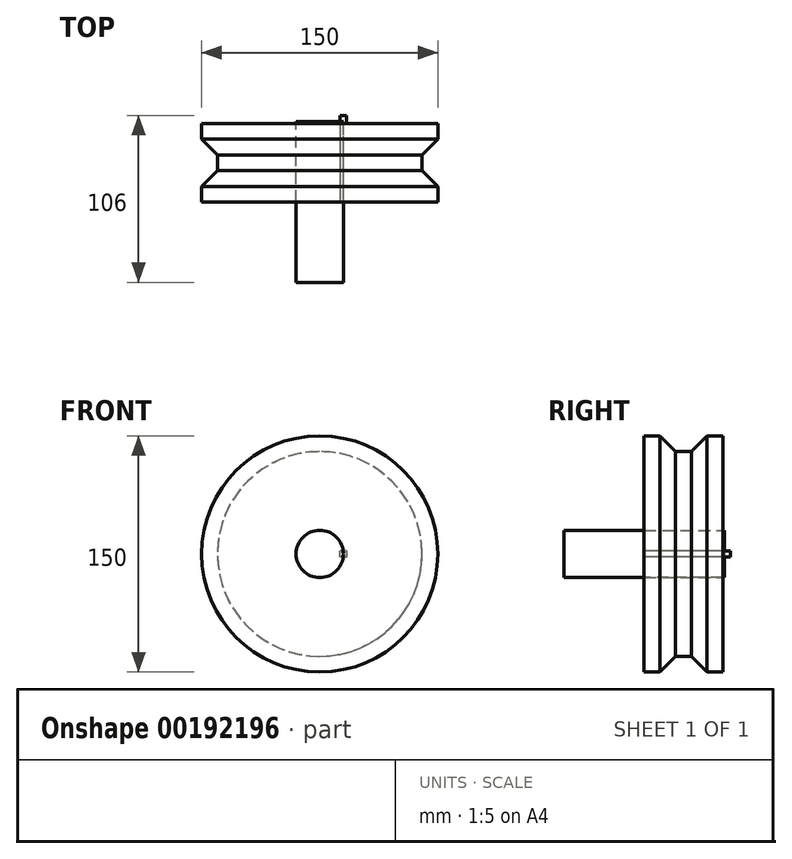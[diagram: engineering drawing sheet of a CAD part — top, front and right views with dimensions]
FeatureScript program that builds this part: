
annotation { "Feature Type Name" : "Feature", "Feature Type Description" : "" }
export const myFeature = defineFeature(function(context is Context, id is Id, definition is map)
    precondition{}
    {
        {
            var Q0;
            Q0=qCreatedBy(makeId("Front.planeOp"),FACE);
            var sketch = newSketch(context, id + "F0", { "sketchPlane" : qUnion([Q0])});
            skCircle(sketch, "E0", {"center": v(0, 0) * mm, "radius": 65 * mm});
            skSolve(sketch);
        }
        {
            var Q0;
            Q0 = qSketchRegion(id + "F0", true);
            var Q1;
            Q1 = qSketchRegion(id + "F4", true);
            extrude(context, id + "F1", {"entities" : qUnion([Q0, Q1]), "depth" : 10 * mm, "symmetric" : true});
        }
        {
            var Q0;
            Q0=makeQuery(id+"F1.opExtrude","CAP_FACE",FACE,{"disambiguationData":[OSD([sQuery(id+"F0.wireOp",EDGE,"E0")])],"isStart":false});
            var sketch = newSketch(context, id + "F2", { "sketchPlane" : qUnion([Q0])});
            skCircle(sketch, "E1", {"center": v(0, 0) * mm, "radius": 75 * mm});
            skSolve(sketch);
        }
        {
            var Q0;
            Q0 = qSketchRegion(id + "F2", true);
            extrude(context, id + "F3", {"entities" : qUnion([Q0]), "operationType" : NewBodyOperationType.ADD, "depth" : 20 * mm});
        }
        {
            var Q0;
            Q0=makeQuery(id+"F1.opExtrude","CAP_FACE",FACE,{"disambiguationData":[OSD([sQuery(id+"F0.wireOp",EDGE,"E0")])],"isStart":true});
            var sketch = newSketch(context, id + "F4", { "sketchPlane" : qUnion([Q0])});
            skCircle(sketch, "E2", {"center": v(0, 0) * mm, "radius": 75 * mm});
            skSolve(sketch);
        }
        {
            var Q0;
            Q0 = qSketchRegion(id + "F4", true);
            extrude(context, id + "F5", {"entities" : qUnion([Q0]), "operationType" : NewBodyOperationType.ADD, "depth" : 20 * mm});
        }
        {
            var Q0;
            Q0=makeQuery(id+"F3.opExtrude","CAP_EDGE",EDGE,{"disambiguationData":[OSD([sQuery(id+"F2.wireOp",EDGE,"E1")])],"isStart":true});
            var Q1;
            Q1=makeQuery(id+"F5.opExtrude","CAP_EDGE",EDGE,{"disambiguationData":[OSD([sQuery(id+"F4.wireOp",EDGE,"E2")])],"isStart":true});
            chamfer(context, id + "F6", {"entities" : qUnion([Q0, Q1]), "width" : 10 * mm, "tangentPropagation" : true});
        }
        {
            var Q0;
            Q0=makeQuery(id+"F3.opExtrude","CAP_FACE",FACE,{"disambiguationData":[OSD([sQuery(id+"F2.wireOp",EDGE,"E1")])],"isStart":false});
            var sketch = newSketch(context, id + "F7", { "sketchPlane" : qUnion([Q0])});
            skCircle(sketch, "E3", {"center": v(0, 0) * mm, "radius": 15 * mm});
            skSolve(sketch);
        }
        {
            var Q0;
            Q0 = qSketchRegion(id + "F7", true);
            extrude(context, id + "F8", {"entities" : qUnion([Q0]), "operationType" : NewBodyOperationType.REMOVE, "oppositeDirection" : true, "depth" : 53.4 * mm});
        }
        {
            var Q0;
            Q0=makeQuery(id+"F3.opExtrude","CAP_FACE",FACE,{"disambiguationData":[OSD([sQuery(id+"F2.wireOp",EDGE,"E1")])],"isStart":false});
            var sketch = newSketch(context, id + "F9", { "sketchPlane" : qUnion([Q0])});
            skLineSegment(sketch, "E4.bottom", {"start": v(17, -2) * mm, "end": v(13, -2) * mm});
            skLineSegment(sketch, "E4.top", {"start": v(17, 2) * mm, "end": v(13, 2) * mm});
            skLineSegment(sketch, "E4.left", {"start": v(17, -2) * mm, "end": v(17, 2) * mm});
            skLineSegment(sketch, "E4.right", {"start": v(13, -2) * mm, "end": v(13, 2) * mm});
            skPoint(sketch, "E4.middle", {"position": v(15, 0) * mm});
            skSolve(sketch);
        }
        {
            var Q0;
            Q0 = qSketchRegion(id + "F9", true);
            extrude(context, id + "F10", {"entities" : qUnion([Q0]), "operationType" : NewBodyOperationType.ADD, "oppositeDirection" : true, "depth" : 55 * mm});
        }
        {
            var Q0;
            Q0=makeQuery(id+"F10.boolean.opBoolean","MERGE",FACE,{"derivedFrom":[makeQuery(id+"F3.opExtrude","CAP_FACE",FACE,{"disambiguationData":[OSD([sQuery(id+"F2.wireOp",EDGE,"E1")])],"isStart":false}),makeQuery(id+"F10.opExtrude","CAP_FACE",FACE,{"disambiguationData":[OSD([sQuery(id+"F9.wireOp",EDGE,"E4.bottom"),sQuery(id+"F9.wireOp",EDGE,"E4.top"),sQuery(id+"F9.wireOp",EDGE,"E4.left"),sQuery(id+"F9.wireOp",EDGE,"E4.right")])],"isStart":true})]});
            var sketch = newSketch(context, id + "F11", { "sketchPlane" : qUnion([Q0])});
            skCircle(sketch, "E5", {"center": v(0, 0) * mm, "radius": 15 * mm});
            skSolve(sketch);
        }
        {
            var Q0;
            Q0 = qSketchRegion(id + "F11", true);
            extrude(context, id + "F12", {"entities" : qUnion([Q0]), "depth" : 102 * mm, "symmetric" : true});
        }
    });
